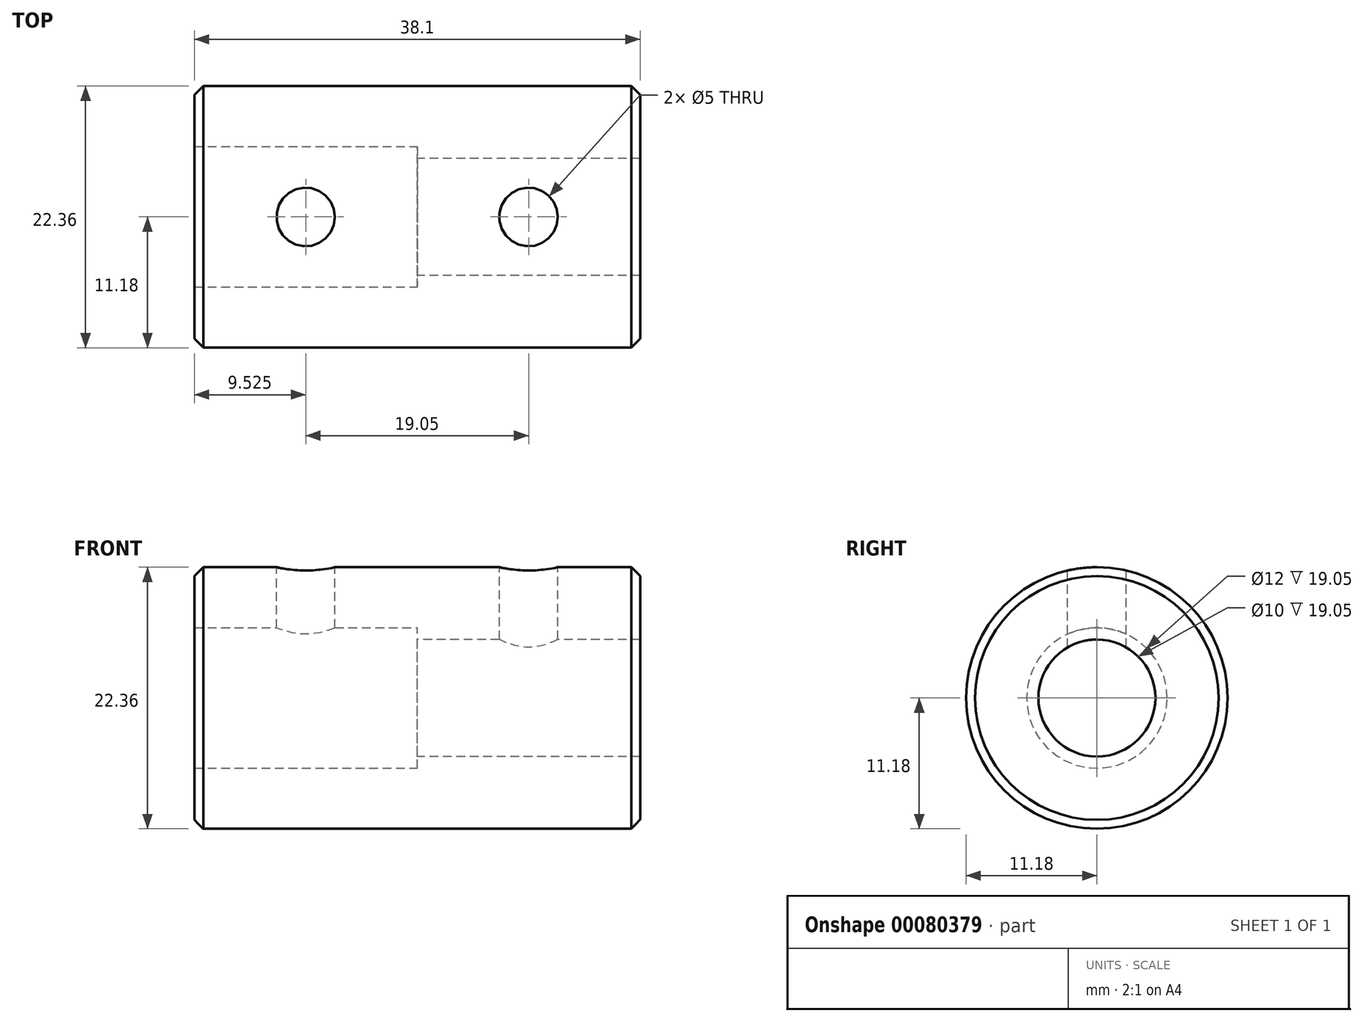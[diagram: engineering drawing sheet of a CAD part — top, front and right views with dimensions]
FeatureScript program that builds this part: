
annotation { "Feature Type Name" : "Feature", "Feature Type Description" : "" }
export const myFeature = defineFeature(function(context is Context, id is Id, definition is map)
    precondition{}
    {
        {
            var Q0;
            Q0=qCreatedBy(makeId("Right.planeOp"),FACE);
            var sketch = newSketch(context, id + "F0", { "sketchPlane" : qUnion([Q0])});
            skCircle(sketch, "E0", {"center": v(0, 0) * mm, "radius": 6 * mm});
            skCircle(sketch, "E1", {"center": v(0, 0) * mm, "radius": 11.18 * mm});
            skSolve(sketch);
        }
        {
            var Q0;
            Q0 = qSketchRegion(id + "F0", true);
            extrude(context, id + "F1", {"entities" : qUnion([Q0]), "oppositeDirection" : true, "depth" : 19.05 * mm});
        }
        {
            var Q0;
            Q0=qCreatedBy(makeId("Right.planeOp"),FACE);
            var sketch = newSketch(context, id + "F2", { "sketchPlane" : qUnion([Q0])});
            skCircle(sketch, "E2.0", {"center": v(0, 0) * mm, "radius": 11.18 * mm});
            skCircle(sketch, "E3", {"center": v(0, 0) * mm, "radius": 5 * mm});
            skSolve(sketch);
        }
        {
            var Q0;
            Q0 = qSketchRegion(id + "F2", true);
            extrude(context, id + "F3", {"entities" : qUnion([Q0]), "operationType" : NewBodyOperationType.ADD, "depth" : 19.05 * mm});
        }
        {
            var Q0;
            Q0=makeQuery(id+"F1.opExtrude","CAP_EDGE",EDGE,{"disambiguationData":[OSD([sQuery(id+"F0.wireOp",EDGE,"E1")])],"isStart":false});
            var Q1;
            Q1=makeQuery(id+"F3.opExtrude","CAP_EDGE",EDGE,{"disambiguationData":[OSD([sQuery(id+"F2.wireOp",EDGE,"E2.0")])],"isStart":false});
            chamfer(context, id + "F4", {"entities" : qUnion([Q0, Q1]), "width" : 0.76 * mm, "tangentPropagation" : true});
        }
        {
            var Q0;
            Q0=qCreatedBy(makeId("Top.planeOp"),FACE);
            cPlane(context, id + "F5", {"entities" : qUnion([Q0]), "cplaneType" : CPlaneType.OFFSET, "offset" : 11.18 * mm, "width" : 152.4 * mm, "height" : 152.4 * mm});
        }
        {
            var Q0;
            Q0=qCreatedBy(id+"F5.planeOp",FACE);
            var sketch = newSketch(context, id + "F6", { "sketchPlane" : qUnion([Q0])});
            skLineSegment(sketch, "E4", {"start": v(-18.29, 11.18) * mm, "end": v(18.29, 11.18) * mm, "construction": true});
            skLineSegment(sketch, "E5", {"start": v(18.29, -11.18) * mm, "end": v(-18.29, -11.18) * mm, "construction": true});
            skLineSegment(sketch, "E6.0", {"start": v(-19.05, -10.41) * mm, "end": v(-19.05, 10.41) * mm, "construction": true});
            skLineSegment(sketch, "E7.0", {"start": v(19.05, 10.41) * mm, "end": v(19.05, -10.41) * mm, "construction": true});
            skLineSegment(sketch, "E8.0", {"start": v(0, 6) * mm, "end": v(0, -6) * mm, "construction": true});
            skLineSegment(sketch, "E9", {"start": v(-46.96, 0) * mm, "end": v(42.12, 0) * mm, "construction": true});
            skLineSegment(sketch, "E10.0", {"start": v(-9.53, 6) * mm, "end": v(-9.53, -6) * mm, "construction": true});
            skLineSegment(sketch, "E11.0", {"start": v(9.53, 6) * mm, "end": v(9.53, -6) * mm, "construction": true});
            skPoint(sketch, "E12", {"position": v(-9.53, 0) * mm});
            skPoint(sketch, "E13", {"position": v(9.53, 0) * mm});
            skSolve(sketch);
        }
        {
            var Q0;
            Q0=sQuery(id+"F6.wireOp",VERTEX,"E12");
            var Q1;
            Q1=sQuery(id+"F6.wireOp",VERTEX,"E13");
            var Q2;
            Q2=makeQuery(id+"F1.opExtrude","SWEPT_BODY",BODY,{"disambiguationData":[OSD([sQuery(id+"F0.wireOp",EDGE,"E0"),sQuery(id+"F0.wireOp",EDGE,"E1")])]});
            hole(context, id + "F7", {"style" : HoleStyle.SIMPLE, "endStyle" : HoleEndStyle.BLIND, "standardTappedOrClearance" : lookupTablePath({ "standard" : "ISO", "engagement" : "75%", "pitch" : "1 mm", "size" : "M6", "type" : "Tapped" }), "standardBlindInLast" : lookupTablePath({ "standard" : "ISO", "engagement" : "75%", "pitch" : "1 mm", "size" : "M6", "type" : "Tapped" }), "holeDiameter" : 5 * mm, "holeDepth" : 12.7 * mm, "locations" : qUnion([Q0, Q1]), "scope" : qUnion([Q2]), "majorDiameter" : 6 * mm});
        }
    });
